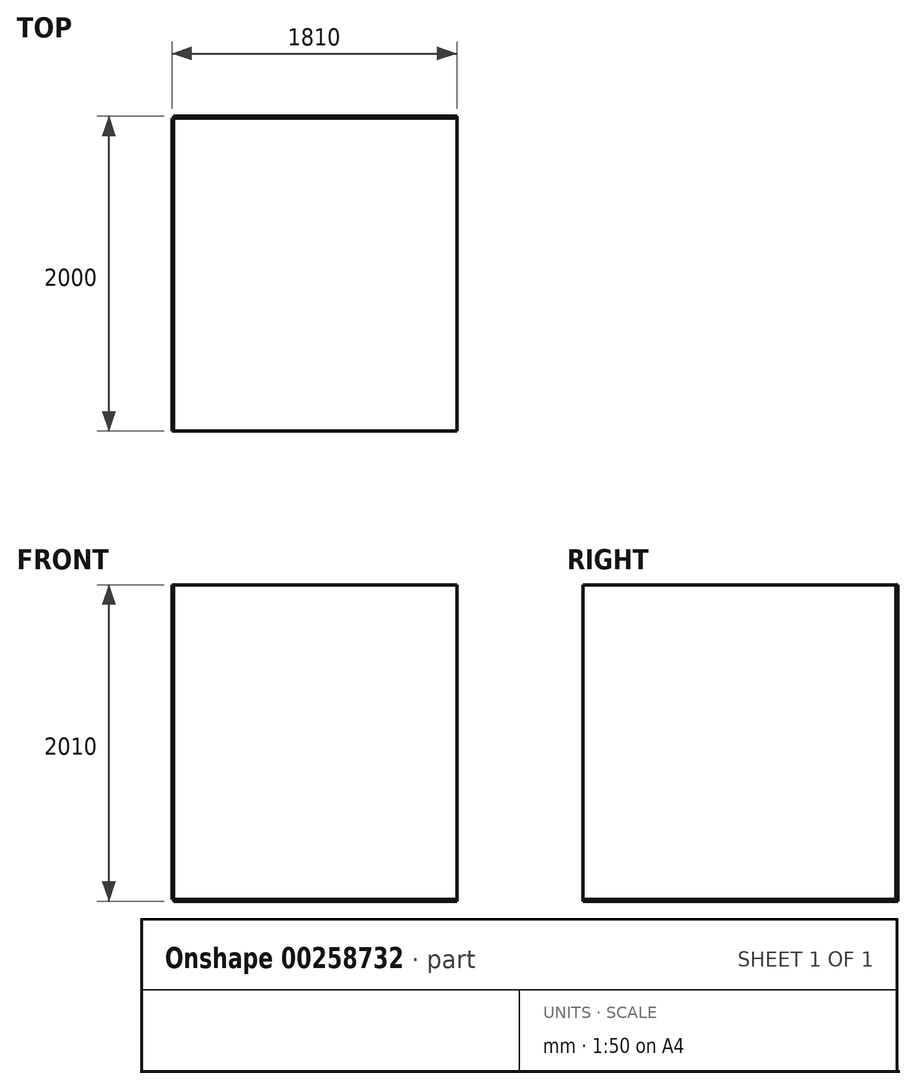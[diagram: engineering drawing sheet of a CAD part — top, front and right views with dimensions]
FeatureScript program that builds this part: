
annotation { "Feature Type Name" : "Feature", "Feature Type Description" : "" }
export const myFeature = defineFeature(function(context is Context, id is Id, definition is map)
    precondition{}
    {
        {
            var Q0;
            Q0=qCreatedBy(makeId("Front.planeOp"),FACE);
            var sketch = newSketch(context, id + "F2", { "sketchPlane" : qUnion([Q0])});
            skLineSegment(sketch, "E0.bottom", {"start": v(0, 0) * mm, "end": v(1800, 0) * mm});
            skLineSegment(sketch, "E0.top", {"start": v(0, 2000) * mm, "end": v(1800, 2000) * mm});
            skLineSegment(sketch, "E0.left", {"start": v(0, 0) * mm, "end": v(0, 2000) * mm});
            skLineSegment(sketch, "E0.right", {"start": v(1800, 0) * mm, "end": v(1800, 2000) * mm});
            skSolve(sketch);
        }
        {
            var Q0;
            Q0 = qSketchRegion(id + "F2", true);
            extrude(context, id + "F3", {"entities" : qUnion([Q0]), "depth" : 10 * mm});
        }
        {
            var Q0;
            Q0=qCreatedBy(makeId("Top.planeOp"),FACE);
            var sketch = newSketch(context, id + "F0", { "sketchPlane" : qUnion([Q0])});
            skLineSegment(sketch, "E1.bottom", {"start": v(0, 0) * mm, "end": v(1800, 0) * mm});
            skLineSegment(sketch, "E1.top", {"start": v(0, -2000) * mm, "end": v(1800, -2000) * mm});
            skLineSegment(sketch, "E1.left", {"start": v(0, 0) * mm, "end": v(0, -2000) * mm});
            skLineSegment(sketch, "E1.right", {"start": v(1800, 0) * mm, "end": v(1800, -2000) * mm});
            skSolve(sketch);
        }
        {
            var Q0;
            Q0=makeQuery(id+"F0.imprint","IMPRINT",FACE,{"disambiguationData":[TD([[makeQuery(id+"F0.imprint","IMPRINT",EDGE,{"derivedFrom":sQuery(id+"F0.wireOp",EDGE,"E1.bottom")}),-1.0]])]});
            extrude(context, id + "F4", {"entities" : qUnion([Q0]), "operationType" : NewBodyOperationType.ADD, "oppositeDirection" : true, "depth" : 10 * mm});
        }
        {
            var Q0;
            Q0=makeQuery(id+"F4.boolean.opBoolean","MERGE",FACE,{"derivedFrom":[makeQuery(id+"F3.opExtrude","SWEPT_FACE",FACE,{"disambiguationData":[OSD([sQuery(id+"F2.wireOp",EDGE,"E0.left")])]}),makeQuery(id+"F4.opExtrude","SWEPT_FACE",FACE,{"disambiguationData":[OSD([sQuery(id+"F0.wireOp",EDGE,"E1.left")])]})]});
            var sketch = newSketch(context, id + "F5", { "sketchPlane" : qUnion([Q0])});
            skLineSegment(sketch, "E2.0", {"start": v(0, -10) * mm, "end": v(0, 2000) * mm});
            skLineSegment(sketch, "E3.0", {"start": v(0, -10) * mm, "end": v(2000, -10) * mm});
            skLineSegment(sketch, "E4.top", {"start": v(0, 2000) * mm, "end": v(2000, 2000) * mm});
            skLineSegment(sketch, "E4.right", {"start": v(2000, -10) * mm, "end": v(2000, 2000) * mm});
            skSolve(sketch);
        }
        {
            var Q0;
            {var subQ1=makeQuery(id+"F3.opExtrude","CAP_EDGE",EDGE,{"disambiguationData":[OSD([sQuery(id+"F2.wireOp",EDGE,"E0.left")])],"isStart":false});Q0=makeQuery(id+"F5.imprint","IMPRINT",FACE,{"disambiguationData":[TD([[makeQuery(id+"F5.imprint","IMPRINT",EDGE,{"derivedFrom":subQ1}),-1.0]])]});}
            extrude(context, id + "F1", {"entities" : qUnion([Q0]), "depth" : 10 * mm});
        }
    });
